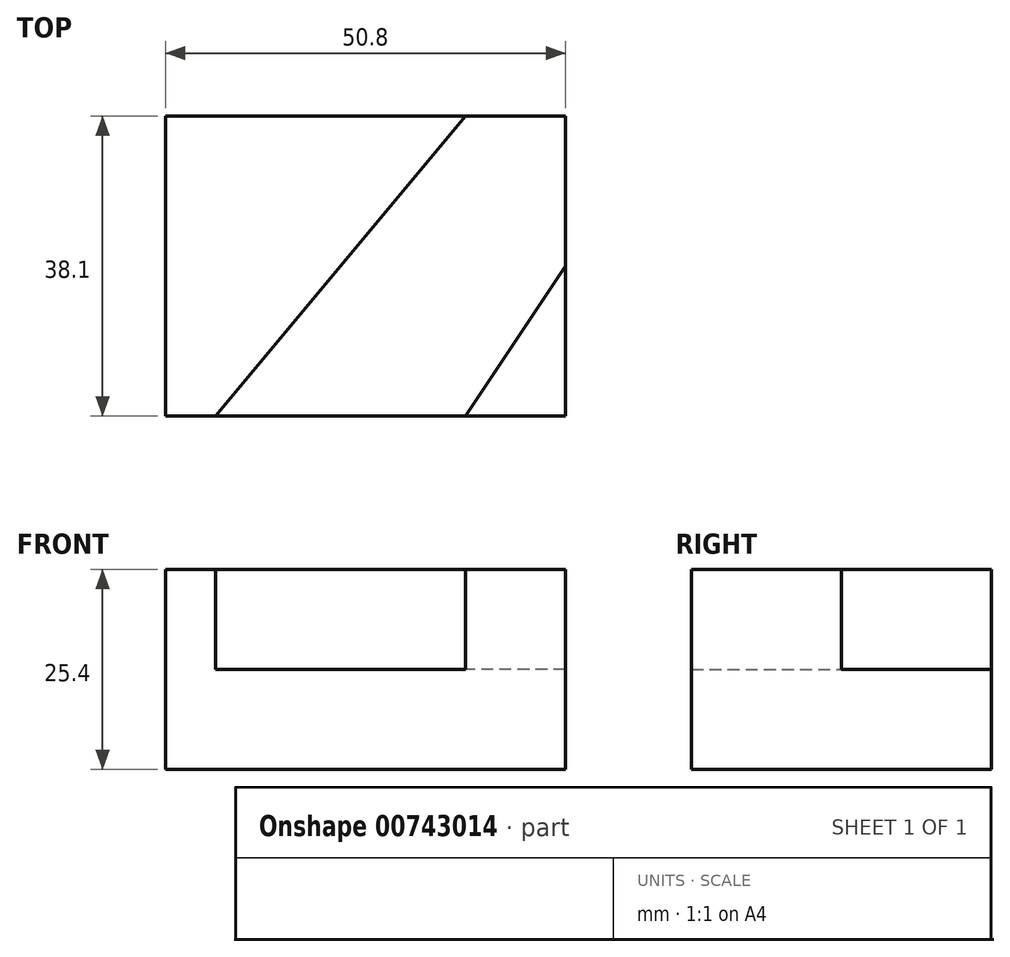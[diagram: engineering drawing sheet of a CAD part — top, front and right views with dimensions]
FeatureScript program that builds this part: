
annotation { "Feature Type Name" : "Feature", "Feature Type Description" : "" }
export const myFeature = defineFeature(function(context is Context, id is Id, definition is map)
    precondition{}
    {
        {
            var Q0;
            Q0=qCreatedBy(makeId("Front.planeOp"),FACE);
            var sketch = newSketch(context, id + "F0", { "sketchPlane" : qUnion([Q0])});
            skLineSegment(sketch, "E0", {"start": v(0, 0) * mm, "end": v(50.8, 0) * mm});
            skLineSegment(sketch, "E1", {"start": v(50.8, 0) * mm, "end": v(50.8, 25.4) * mm});
            skLineSegment(sketch, "E2", {"start": v(50.8, 25.4) * mm, "end": v(0, 25.4) * mm});
            skLineSegment(sketch, "E3", {"start": v(0, 25.4) * mm, "end": v(0, 0) * mm});
            skSolve(sketch);
        }
        {
            var Q0;
            Q0=makeQuery(id+"F0.imprint","IMPRINT",FACE,{"disambiguationData":[TD([[makeQuery(id+"F0.imprint","IMPRINT",EDGE,{"derivedFrom":sQuery(id+"F0.wireOp",EDGE,"E0")}),1.0]])]});
            extrude(context, id + "F1", {"entities" : qUnion([Q0]), "depth" : 38.1 * mm, "offsetDistance" : 25.4 * mm});
        }
        {
            var Q0;
            Q0=makeQuery(id+"F1.opExtrude","SWEPT_FACE",FACE,{"disambiguationData":[OSD([sQuery(id+"F0.wireOp",EDGE,"E2")])]});
            var sketch = newSketch(context, id + "F2", { "sketchPlane" : qUnion([Q0])});
            skLineSegment(sketch, "E4", {"start": v(38.1, -38.1) * mm, "end": v(50.8, -19.05) * mm});
            skLineSegment(sketch, "E5", {"start": v(50.8, -19.05) * mm, "end": v(50.8, -38.1) * mm});
            skLineSegment(sketch, "E6", {"start": v(50.8, -38.1) * mm, "end": v(38.1, -38.1) * mm});
            skLineSegment(sketch, "E7", {"start": v(0, -31.75) * mm, "end": v(38.1, 0) * mm});
            skLineSegment(sketch, "E8", {"start": v(38.1, 0) * mm, "end": v(0, 0) * mm});
            skLineSegment(sketch, "E9", {"start": v(0, 0) * mm, "end": v(0, -31.75) * mm});
            skSolve(sketch);
        }
        {
            var Q0;
            {var subQ8=sQuery(id+"F2.wireOp",EDGE,"E4");Q0=makeQuery(id+"F2.imprint","IMPRINT",FACE,{"disambiguationData":[TD([[makeQuery(id+"F2.imprint","IMPRINT",EDGE,{"derivedFrom":subQ8}),1.0]])]});}
            extrude(context, id + "F3", {"entities" : qUnion([Q0]), "operationType" : NewBodyOperationType.REMOVE, "oppositeDirection" : true, "depth" : 12.7 * mm, "offsetDistance" : 25.4 * mm});
        }
        {
            var Q0;
            Q0=makeQuery(id+"F3.boolean.opBoolean","COPY",FACE,{"derivedFrom":makeQuery(id+"F3.opExtrude","CAP_FACE",FACE,{"disambiguationData":[OSD([sQuery(id+"F0.wireOp",EDGE,"E1"),sQuery(id+"F0.wireOp",EDGE,"E2"),sQuery(id+"F0.wireOp",EDGE,"E3"),sQuery(id+"F2.wireOp",EDGE,"E4"),sQuery(id+"F2.wireOp",EDGE,"E7")])],"isStart":false})});
            var sketch = newSketch(context, id + "F4", { "sketchPlane" : qUnion([Q0])});
            skLineSegment(sketch, "E10", {"start": v(6.35, -38.1) * mm, "end": v(38.1, 0) * mm});
            skLineSegment(sketch, "E11", {"start": v(38.1, 0) * mm, "end": v(50.8, 0) * mm});
            skLineSegment(sketch, "E12", {"start": v(50.8, 0) * mm, "end": v(50.8, -19.05) * mm});
            skLineSegment(sketch, "E13", {"start": v(50.8, -19.05) * mm, "end": v(38.1, -38.1) * mm});
            skLineSegment(sketch, "E14", {"start": v(38.1, -38.1) * mm, "end": v(6.35, -38.1) * mm});
            skSolve(sketch);
        }
        {
            var Q0;
            {var subQ0=sQuery(id+"F4.wireOp",EDGE,"E10");Q0=makeQuery(id+"F4.imprint","IMPRINT",FACE,{"disambiguationData":[TD([[makeQuery(id+"F4.imprint","IMPRINT",EDGE,{"derivedFrom":subQ0}),1.0]])]});}
            extrude(context, id + "F5", {"entities" : qUnion([Q0]), "operationType" : NewBodyOperationType.ADD, "depth" : 12.7 * mm, "offsetDistance" : 25.4 * mm});
        }
    });
